FREECAD ASSEMBLY — COMPONENT RECIPES ("clip-on_shades_case_assembly")

This assembly document has 3 components, labeled P0..P2 below (a component is one placed body or linked part). 0 of them carry a construction recipe — the FreeCAD feature program that regenerates the part from scratch, quoted from this document or its linked companion documents; the rest are supplied as boundary geometry only. No exploded tour is included for this assembly.
COMPONENT P0 — geometry summary ("Clip-on shades"; no construction recipe available for this part):
  bounding box: 114.7 x 42.6 x 6.7 mm
  tessellated surface: 6,176 triangles
  volume: 2359 mm^3 (7% of its bounding box)
  symmetry: mirror-symmetric across its x mid-plane
COMPONENT P1 — geometry summary ("Clip-on shades case bottom"; no construction recipe available for this part):
  bounding box: 131.9 x 56.5 x 13.0 mm
  tessellated surface: 37,842 triangles
  volume: 28965 mm^3 (30% of its bounding box)
COMPONENT P2 — geometry summary ("Clip-on shades case top"; no construction recipe available for this part):
  bounding box: 131.9 x 56.5 x 9.6 mm
  tessellated surface: 37,618 triangles
  volume: 19473 mm^3 (27% of its bounding box)
PROVENANCE & LICENSES
A FreeCAD (.FCStd) document from a public repository crawl; recipes are the document's own serialized feature recipes (and, for linked parts, companion documents' recipes).
License: mit.
